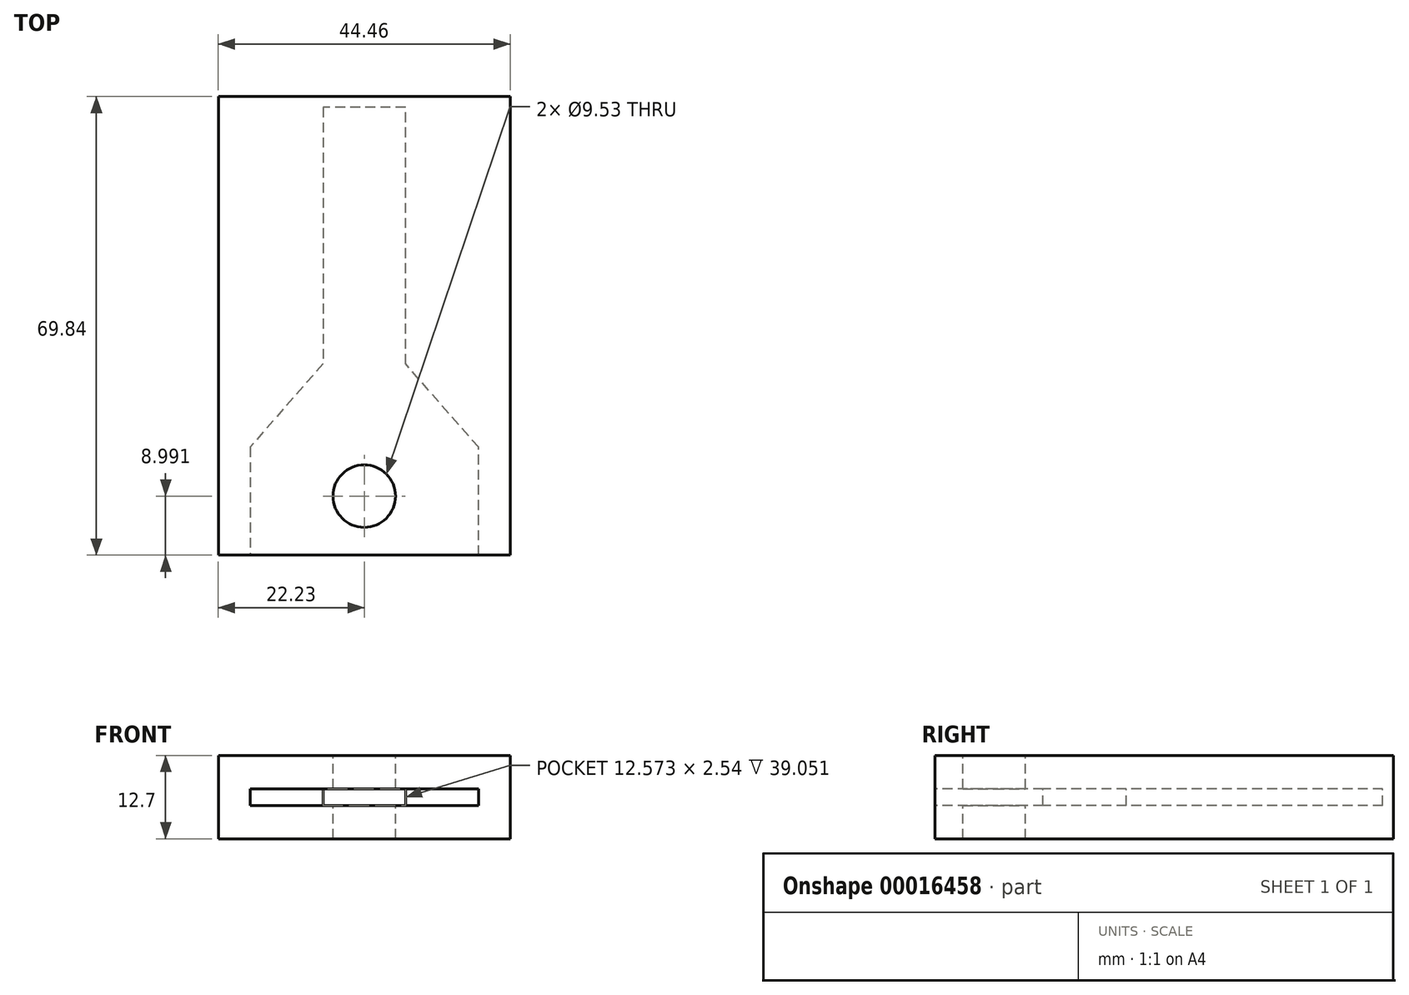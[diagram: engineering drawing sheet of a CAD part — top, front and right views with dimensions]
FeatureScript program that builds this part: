
annotation { "Feature Type Name" : "Feature", "Feature Type Description" : "" }
export const myFeature = defineFeature(function(context is Context, id is Id, definition is map)
    precondition{}
    {
        {
            var Q0;
            Q0=qCreatedBy(makeId("Top.planeOp"),FACE);
            var sketch = newSketch(context, id + "F0", { "sketchPlane" : qUnion([Q0])});
            skLineSegment(sketch, "E0", {"start": v(-15.88, 0) * mm, "end": v(-15.88, 12.7) * mm});
            skLineSegment(sketch, "E1", {"start": v(-15.87, 12.7) * mm, "end": v(-4.76, 25.4) * mm});
            skLineSegment(sketch, "E2", {"start": v(-4.76, 25.4) * mm, "end": v(-4.76, 63.5) * mm});
            skLineSegment(sketch, "E3", {"start": v(-4.76, 63.5) * mm, "end": v(0, 63.5) * mm});
            skLineSegment(sketch, "E4", {"start": v(-15.88, 0) * mm, "end": v(0, 0) * mm});
            skLineSegment(sketch, "E5", {"start": v(0, 7.94) * mm, "end": v(-6.35, 7.94) * mm});
            skLineSegment(sketch, "E6", {"start": v(-6.35, 7.94) * mm, "end": v(0, 3.17) * mm});
            skLineSegment(sketch, "E7.MirrorCS", {"start": v(4.76, 63.5) * mm, "end": v(0, 63.5) * mm});
            skLineSegment(sketch, "E8.MirrorCS", {"start": v(4.76, 25.4) * mm, "end": v(4.76, 63.5) * mm});
            skLineSegment(sketch, "E9.MirrorCS", {"start": v(15.88, 0) * mm, "end": v(0, 0) * mm});
            skLineSegment(sketch, "E10.MirrorCS", {"start": v(15.88, 0) * mm, "end": v(15.88, 12.7) * mm});
            skLineSegment(sketch, "E11.MirrorCS", {"start": v(6.35, 7.94) * mm, "end": v(0, 3.17) * mm});
            skLineSegment(sketch, "E12.MirrorCS", {"start": v(15.88, 12.7) * mm, "end": v(4.76, 25.4) * mm});
            skLineSegment(sketch, "E13.MirrorCS", {"start": v(0, 7.94) * mm, "end": v(6.35, 7.94) * mm});
            skLineSegment(sketch, "E14", {"start": v(0, 63.5) * mm, "end": v(0, 0) * mm, "construction": true});
            skPoint(sketch, "E15", {"position": v(0, 31.75) * mm});
            skSolve(sketch);
        }
        {
            var Q0;
            Q0 = qSketchRegion(id + "F0", true);
            extrude(context, id + "F1", {"entities" : qUnion([Q0]), "endBound" : BoundingType.SYMMETRIC, "depth" : 1.59 * mm});
        }
        {
            var Q0;
            Q0=qCreatedBy(makeId("Top.planeOp"),FACE);
            var sketch = newSketch(context, id + "F2", { "sketchPlane" : qUnion([Q0])});
            skLineSegment(sketch, "E16.bottom", {"start": v(-22.23, 66.67) * mm, "end": v(22.23, 66.68) * mm});
            skLineSegment(sketch, "E16.top", {"start": v(-22.23, -3.17) * mm, "end": v(22.23, -3.17) * mm});
            skLineSegment(sketch, "E16.left", {"start": v(-22.23, 66.67) * mm, "end": v(-22.23, -3.18) * mm});
            skLineSegment(sketch, "E16.right", {"start": v(22.23, 66.67) * mm, "end": v(22.23, -3.17) * mm});
            skLineSegment(sketch, "E17", {"start": v(0, 66.67) * mm, "end": v(0, -3.17) * mm, "construction": true});
            skPoint(sketch, "E18", {"position": v(0, 31.75) * mm});
            skSolve(sketch);
        }
        {
            var Q0;
            Q0 = qSketchRegion(id + "F2", true);
            extrude(context, id + "F3", {"entities" : qUnion([Q0]), "endBound" : BoundingType.SYMMETRIC, "depth" : 12.7 * mm});
        }
        {
            var Q0;
            Q0=qCreatedBy(makeId("Top.planeOp"),FACE);
            var sketch = newSketch(context, id + "F4", { "sketchPlane" : qUnion([Q0])});
            skLineSegment(sketch, "E19.0", {"start": v(-6.29, 25.97) * mm, "end": v(-17.4, 13.27) * mm});
            skLineSegment(sketch, "E19.1", {"start": v(-6.29, 65.02) * mm, "end": v(-6.29, 25.97) * mm});
            skLineSegment(sketch, "E19.2", {"start": v(6.29, 65.02) * mm, "end": v(-6.29, 65.02) * mm});
            skLineSegment(sketch, "E19.4", {"start": v(6.29, 25.97) * mm, "end": v(6.29, 65.02) * mm});
            skLineSegment(sketch, "E19.5", {"start": v(-17.4, 13.27) * mm, "end": v(-17.4, -3.17) * mm});
            skLineSegment(sketch, "E19.6", {"start": v(17.4, 13.27) * mm, "end": v(6.29, 25.97) * mm});
            skLineSegment(sketch, "E19.7", {"start": v(17.4, -3.17) * mm, "end": v(17.4, 13.27) * mm});
            skLineSegment(sketch, "E20", {"start": v(-17.4, -3.17) * mm, "end": v(17.4, -3.17) * mm});
            skSolve(sketch);
        }
        {
            var Q0;
            Q0 = qSketchRegion(id + "F4", true);
            extrude(context, id + "F5", {"entities" : qUnion([Q0]), "operationType" : NewBodyOperationType.REMOVE, "endBound" : BoundingType.SYMMETRIC, "oppositeDirection" : true, "depth" : 2.54 * mm});
        }
        {
            var Q0;
            Q0=qCreatedBy(makeId("Top.planeOp"),FACE);
            var sketch = newSketch(context, id + "F6", { "sketchPlane" : qUnion([Q0])});
            skCircle(sketch, "E21", {"center": v(0, 5.82) * mm, "radius": 2.12 * mm, "construction": true});
            skCircle(sketch, "E22", {"center": v(0, 5.82) * mm, "radius": 4.76 * mm});
            skSolve(sketch);
        }
        {
            var Q0;
            Q0 = qSketchRegion(id + "F6", true);
            extrude(context, id + "F7", {"entities" : qUnion([Q0]), "operationType" : NewBodyOperationType.REMOVE, "endBound" : BoundingType.SYMMETRIC, "oppositeDirection" : true, "depth" : 50.8 * mm});
        }
    });
